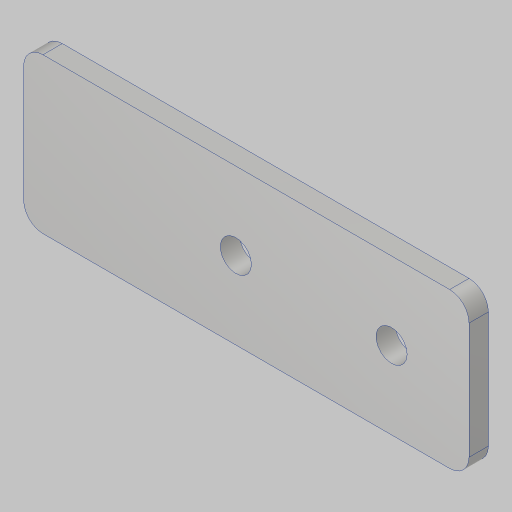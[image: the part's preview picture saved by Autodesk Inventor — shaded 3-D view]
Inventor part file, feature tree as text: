
AUTODESK INVENTOR PART (.ipt)
format: ipt  version: 2023.5 (Build 275446000, 446)  size: 119,808 bytes
history: native  units: in
note: dims shown in document units (in); Inventor stores cm internally (conversion verified against a paired STEP export)
features: sketch x2, extrude x1, hole x1, fillet x1
ambient origin geometry x8: Origin, YZ Plane, XZ Plane, XY Plane, X Axis, Y Axis, Z Axis, Center Point
bodies: Solid1 (feature_tree)
feature tree (5):
  extrude  "Extrusion1"  Depth=2.875in
  hole  "Hole2"  [1 undecoded]
  fillet  "Fillet2"  Radius=0.125in
  sketch  "Sketch1"  dims[d2=0.125in d3=0.0in d15=2.875in]
  sketch  "Sketch3"  dims[d16=1.0in d17=1.005in d19=0.201in d20=0.75in d21=0.385in d22=0.25in d23=0.5635in d24=1.0in d25=0.8108in d26=0.125in d27=0.5in]
note: 1 required parameter value undecoded (feature->parameter linkage not recoverable at this tier; creation-order binding heuristic only, values carry confidence <= 0.55)
